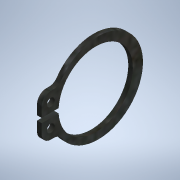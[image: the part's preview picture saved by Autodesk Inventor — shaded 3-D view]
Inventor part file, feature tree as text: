
AUTODESK INVENTOR PART (.ipt)
format: ipt  version: 2021.3 (Build 253353000, 353)  size: 130,560 bytes
history: native  units: mm (DEFAULTED — no unit token found)
features: other x14, extrude x1, sketch x1
ambient origin geometry x8: Origin, YZ Plane, XZ Plane, XY Plane, X Axis, Y Axis, Z Axis, Center Point
bodies: Solid1 (feature_tree)
feature tree (16):
  extrude  "Extrusion1"  TaperAngle=0.0deg  [1 undecoded]
  other  "1_XY"
  other  "1_YZ"
  other  "1_ZX"
  other  "1_X"
  other  "1_Y"
  other  "1_Z"
  other  "1_Center"
  other  "combination_module_XY"
  other  "combination_module_YZ"
  other  "combination_module_ZX"
  other  "combination_module_X"
  other  "combination_module_Y"
  other  "combination_module_Z"
  other  "combination_module_Center"
  sketch  "Sketch_6"  dims[d0=1.0mm d1=0.0mm d2=0.0mm]
note: 1 required parameter value undecoded (feature->parameter linkage not recoverable at this tier; creation-order binding heuristic only, values carry confidence <= 0.55)
